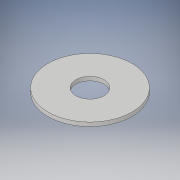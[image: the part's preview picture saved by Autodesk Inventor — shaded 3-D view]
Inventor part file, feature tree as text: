
AUTODESK INVENTOR PART (.ipt)
format: ipt  version: 2017 (Build 210142000, 142)  size: 95,744 bytes
history: native  units: in
note: dims shown in document units (in); Inventor stores cm internally (conversion verified against a paired STEP export)
features: extrude x1, sketch x1
ambient origin geometry x8: Origin, YZ Plane, XZ Plane, XY Plane, X Axis, Y Axis, Z Axis, Center Point
bodies: Solid1 (feature_tree)
feature tree (2):
  extrude  "Extrusion1"  Depth=0.035in
  sketch  "Sketch1"  dims[d0=0.25in d1=0.75in d2=0.035in d3=0.0in]
